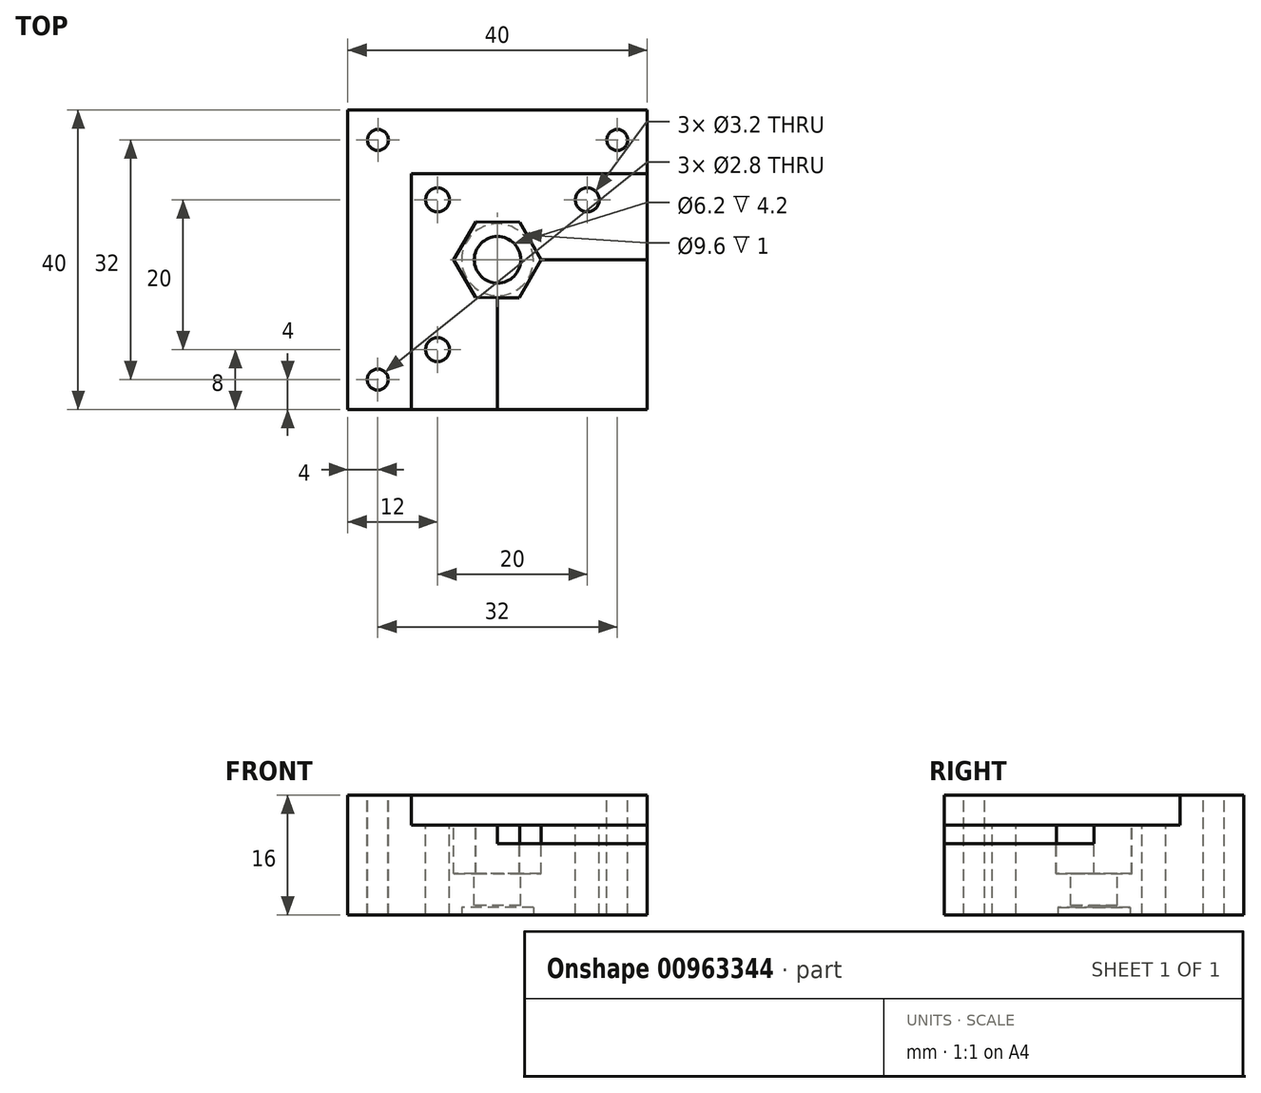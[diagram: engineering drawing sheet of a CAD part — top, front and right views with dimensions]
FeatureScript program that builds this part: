
annotation { "Feature Type Name" : "Feature", "Feature Type Description" : "" }
export const myFeature = defineFeature(function(context is Context, id is Id, definition is map)
    precondition{}
    {
        {
            var Q0;
            Q0=qCreatedBy(makeId("Top.planeOp"),FACE);
            var sketch = newSketch(context, id + "F0", { "sketchPlane" : qUnion([Q0])});
            skLineSegment(sketch, "E0.bottom", {"start": v(20, 20) * mm, "end": v(-20, 20) * mm});
            skLineSegment(sketch, "E0.top", {"start": v(20, -20) * mm, "end": v(-20, -20) * mm});
            skLineSegment(sketch, "E0.left", {"start": v(20, 20) * mm, "end": v(20, -20) * mm});
            skLineSegment(sketch, "E0.right", {"start": v(-20, 20) * mm, "end": v(-20, -20) * mm});
            skPoint(sketch, "E0.middle", {"position": v(0, 0) * mm});
            skSolve(sketch);
        }
        {
            var Q0;
            Q0=makeQuery(id+"F0.imprint","IMPRINT",FACE,{"disambiguationData":[TD([[makeQuery(id+"F0.imprint","IMPRINT",EDGE,{"derivedFrom":sQuery(id+"F0.wireOp",EDGE,"E0.bottom")}),1.0]])]});
            extrude(context, id + "F1", {"entities" : qUnion([Q0]), "oppositeDirection" : true, "depth" : 16 * mm, "offsetDistance" : 25 * mm});
        }
        {
            var Q0;
            Q0=qCreatedBy(makeId("Top.planeOp"),FACE);
            var sketch = newSketch(context, id + "F2", { "sketchPlane" : qUnion([Q0])});
            skCircle(sketch, "E1", {"center": v(0, 0) * mm, "radius": 3.1 * mm});
            skSolve(sketch);
        }
        {
            var Q0;
            Q0=makeQuery(id+"F2.imprint","IMPRINT",FACE,{"disambiguationData":[TD([[makeQuery(id+"F2.imprint","IMPRINT",EDGE,{"derivedFrom":sQuery(id+"F2.wireOp",EDGE,"E1")}),1.0]])]});
            extrude(context, id + "F3", {"entities" : qUnion([Q0]), "operationType" : NewBodyOperationType.REMOVE, "oppositeDirection" : true, "depth" : 14.7 * mm, "offsetDistance" : 25 * mm});
        }
        {
            var Q0;
            Q0=qCreatedBy(makeId("Top.planeOp"),FACE);
            var sketch = newSketch(context, id + "F4", { "sketchPlane" : qUnion([Q0])});
            skLineSegment(sketch, "E2.bottom", {"start": v(20, -20) * mm, "end": v(-11.5, -20) * mm});
            skLineSegment(sketch, "E2.top", {"start": v(20, 11.5) * mm, "end": v(-11.5, 11.5) * mm});
            skLineSegment(sketch, "E2.left", {"start": v(20, -20) * mm, "end": v(20, 11.5) * mm});
            skLineSegment(sketch, "E2.right", {"start": v(-11.5, -20) * mm, "end": v(-11.5, 11.5) * mm});
            skSolve(sketch);
        }
        {
            var Q0;
            Q0=makeQuery(id+"F4.imprint","IMPRINT",FACE,{"disambiguationData":[TD([[makeQuery(id+"F4.imprint","IMPRINT",EDGE,{"derivedFrom":sQuery(id+"F4.wireOp",EDGE,"E2.bottom")}),-1.0]])]});
            extrude(context, id + "F5", {"entities" : qUnion([Q0]), "operationType" : NewBodyOperationType.REMOVE, "oppositeDirection" : true, "depth" : 4 * mm, "offsetDistance" : 25 * mm});
        }
        {
            var Q0;
            Q0=qCreatedBy(makeId("Top.planeOp"),FACE);
            cPlane(context, id + "F6", {"entities" : qUnion([Q0]), "cplaneType" : CPlaneType.OFFSET, "offset" : 3.5 * mm, "oppositeDirection" : true, "width" : 150 * mm, "height" : 150 * mm});
        }
        {
            var Q0;
            Q0=qCreatedBy(id+"F6.planeOp",FACE);
            var sketch = newSketch(context, id + "F7", { "sketchPlane" : qUnion([Q0])});
            skCircle(sketch, "E3.cCircle", {"center": v(0, 0) * mm, "radius": 5.05 * mm, "construction": true});
            skLineSegment(sketch, "E3.0", {"start": v(2.94, 5.04) * mm, "end": v(5.83, -0.03) * mm});
            skLineSegment(sketch, "E3.1", {"start": v(5.83, -0.03) * mm, "end": v(2.9, -5.06) * mm});
            skLineSegment(sketch, "E3.2", {"start": v(2.9, -5.06) * mm, "end": v(-2.94, -5.04) * mm});
            skLineSegment(sketch, "E3.3", {"start": v(-2.94, -5.04) * mm, "end": v(-5.83, 0.03) * mm});
            skLineSegment(sketch, "E3.4", {"start": v(-5.83, 0.03) * mm, "end": v(-2.9, 5.06) * mm});
            skLineSegment(sketch, "E3.5", {"start": v(-2.9, 5.06) * mm, "end": v(2.94, 5.04) * mm});
            skPoint(sketch, "E3.0.midPoint", {"position": v(4.39, 2.5) * mm});
            skSolve(sketch);
        }
        {
            var Q0;
            Q0 = qSketchRegion(id + "F7", true);
            extrude(context, id + "F8", {"entities" : qUnion([Q0]), "operationType" : NewBodyOperationType.REMOVE, "oppositeDirection" : true, "depth" : 7 * mm, "offsetDistance" : 25 * mm});
        }
        {
            var Q0;
            Q0=qCreatedBy(id+"F6.planeOp",FACE);
            var sketch = newSketch(context, id + "F9", { "sketchPlane" : qUnion([Q0])});
            skLineSegment(sketch, "E4.bottom", {"start": v(0, 0) * mm, "end": v(20, 0) * mm});
            skLineSegment(sketch, "E4.top", {"start": v(0, -20) * mm, "end": v(20, -20) * mm});
            skLineSegment(sketch, "E4.left", {"start": v(0, 0) * mm, "end": v(0, -20) * mm});
            skLineSegment(sketch, "E4.right", {"start": v(20, 0) * mm, "end": v(20, -20) * mm});
            skSolve(sketch);
        }
        {
            var Q0;
            Q0 = qSketchRegion(id + "F9", true);
            extrude(context, id + "F10", {"entities" : qUnion([Q0]), "operationType" : NewBodyOperationType.REMOVE, "oppositeDirection" : true, "depth" : 3 * mm, "offsetDistance" : 25 * mm});
        }
        {
            var Q0;
            Q0=qCreatedBy(id+"F6.planeOp",FACE);
            var sketch = newSketch(context, id + "F11", { "sketchPlane" : qUnion([Q0])});
            skCircle(sketch, "E5", {"center": v(-8, 8) * mm, "radius": 1.6 * mm});
            skCircle(sketch, "E6", {"center": v(12, 8) * mm, "radius": 1.6 * mm});
            skCircle(sketch, "E7", {"center": v(-8, -12) * mm, "radius": 1.6 * mm});
            skLineSegment(sketch, "E8", {"start": v(-8, 24.47) * mm, "end": v(-8, -27.35) * mm, "construction": true});
            skLineSegment(sketch, "E9", {"start": v(-25.17, 8) * mm, "end": v(34.53, 8) * mm, "construction": true});
            skSolve(sketch);
        }
        {
            var Q0;
            Q0 = qSketchRegion(id + "F11", true);
            extrude(context, id + "F12", {"entities" : qUnion([Q0]), "operationType" : NewBodyOperationType.REMOVE, "oppositeDirection" : true, "depth" : 25 * mm, "offsetDistance" : 25 * mm});
        }
        {
            var Q0;
            Q0=qCreatedBy(makeId("Top.planeOp"),FACE);
            cPlane(context, id + "F13", {"entities" : qUnion([Q0]), "cplaneType" : CPlaneType.OFFSET, "offset" : 16 * mm, "oppositeDirection" : true, "width" : 150 * mm, "height" : 150 * mm});
        }
        {
            var Q0;
            Q0=qCreatedBy(id+"F13.planeOp",FACE);
            var sketch = newSketch(context, id + "F14", { "sketchPlane" : qUnion([Q0])});
            skCircle(sketch, "E10", {"center": v(0, 0) * mm, "radius": 4.8 * mm});
            skSolve(sketch);
        }
        {
            var Q0;
            Q0 = qSketchRegion(id + "F14", true);
            extrude(context, id + "F15", {"entities" : qUnion([Q0]), "operationType" : NewBodyOperationType.REMOVE, "depth" : 1 * mm, "offsetDistance" : 25 * mm});
        }
        {
            var Q0;
            Q0=qCreatedBy(makeId("Top.planeOp"),FACE);
            var sketch = newSketch(context, id + "F16", { "sketchPlane" : qUnion([Q0])});
            skCircle(sketch, "E11", {"center": v(-15.97, 16) * mm, "radius": 1.4 * mm});
            skCircle(sketch, "E12", {"center": v(16, 16) * mm, "radius": 1.4 * mm});
            skCircle(sketch, "E13", {"center": v(-16, -16) * mm, "radius": 1.4 * mm});
            skLineSegment(sketch, "E14", {"start": v(-16, 26.93) * mm, "end": v(-16, -33.68) * mm, "construction": true});
            skLineSegment(sketch, "E15", {"start": v(-25, 16) * mm, "end": v(39, 16) * mm, "construction": true});
            skSolve(sketch);
        }
        {
            var Q0;
            Q0 = qSketchRegion(id + "F16", true);
            extrude(context, id + "F17", {"entities" : qUnion([Q0]), "operationType" : NewBodyOperationType.REMOVE, "oppositeDirection" : true, "depth" : 25 * mm, "offsetDistance" : 25 * mm});
        }
    });
